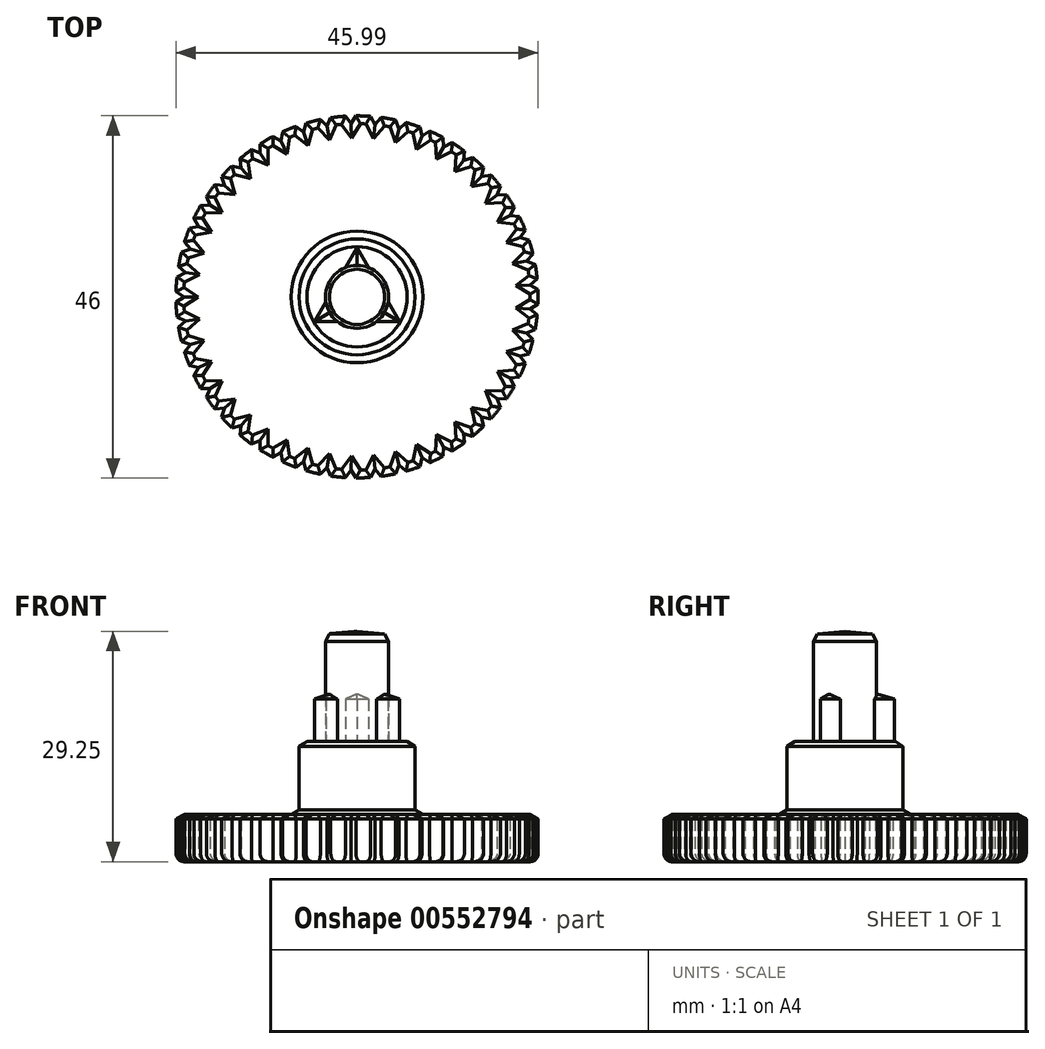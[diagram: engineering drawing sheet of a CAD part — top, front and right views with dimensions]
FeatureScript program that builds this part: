
annotation { "Feature Type Name" : "Feature", "Feature Type Description" : "" }
export const myFeature = defineFeature(function(context is Context, id is Id, definition is map)
    precondition{}
    {
        {
            var Q0;
            Q0=qCreatedBy(makeId("Front.planeOp"),FACE);
            var sketch = newSketch(context, id + "F0", { "sketchPlane" : qUnion([Q0])});
            skPoint(sketch, "E0.0", {"position": v(-5.65, 5.6) * mm});
            skLineSegment(sketch, "E1", {"start": v(-22, -9.25) * mm, "end": v(-22, -15.25) * mm});
            skLineSegment(sketch, "E2", {"start": v(-22, -15.25) * mm, "end": v(0, -15.25) * mm});
            skLineSegment(sketch, "E3", {"start": v(0, -15.25) * mm, "end": v(0, 14) * mm});
            skLineSegment(sketch, "E4", {"start": v(0, 14) * mm, "end": v(-4, 13.67) * mm});
            skLineSegment(sketch, "E5", {"start": v(-4, 13.67) * mm, "end": v(-4, 0) * mm});
            skLineSegment(sketch, "E6", {"start": v(-4, 0) * mm, "end": v(-7.37, 0) * mm});
            skLineSegment(sketch, "E7", {"start": v(-7.37, 0) * mm, "end": v(-7.37, -9.25) * mm});
            skLineSegment(sketch, "E8", {"start": v(-7.37, -9.25) * mm, "end": v(-22, -9.25) * mm});
            skSolve(sketch);
        }
        {
            var Q0;
            Q0=qSketchRegion(id+"F0",true);
            var Q1;
            Q1=sQuery(id+"F0.wireOp",EDGE,"E3");
            revolve(context, id + "F1", {"entities" : qUnion([Q0]), "axis" : qUnion([Q1]), "revolveType" : RevolveType.FULL});
        }
        {
            var Q0;
            Q0=makeQuery(id+"F1.opRevolve","SWEPT_FACE",FACE,{"disambiguationData":[OSD([sQuery(id+"F0.wireOp",EDGE,"E6")])]});
            var sketch = newSketch(context, id + "F2", { "sketchPlane" : qUnion([Q0])});
            skLineSegment(sketch, "E9", {"start": v(1.46, 3.72) * mm, "end": v(0, 6.25) * mm});
            skLineSegment(sketch, "E10", {"start": v(0, 6.25) * mm, "end": v(-1.46, 3.72) * mm});
            skLineSegment(sketch, "E11", {"start": v(-1.46, 3.72) * mm, "end": v(1.46, 3.72) * mm});
            skCircle(sketch, "E12", {"center": v(0, 0) * mm, "radius": 6.25 * mm, "construction": true});
            skCircle(sketch, "E13.0", {"center": v(0, 0) * mm, "radius": 4 * mm, "construction": true});
            skLineSegment(sketch, "E14.1.0", {"start": v(-5.41, -3.12) * mm, "end": v(-2.5, -3.12) * mm});
            skLineSegment(sketch, "E14.1.1", {"start": v(-3.95, -0.6) * mm, "end": v(-5.41, -3.12) * mm});
            skLineSegment(sketch, "E14.1.2", {"start": v(-2.5, -3.12) * mm, "end": v(-3.95, -0.6) * mm});
            skLineSegment(sketch, "E14.2.0", {"start": v(5.41, -3.12) * mm, "end": v(3.95, -0.6) * mm});
            skLineSegment(sketch, "E14.2.1", {"start": v(2.5, -3.12) * mm, "end": v(5.41, -3.12) * mm});
            skLineSegment(sketch, "E14.2.2", {"start": v(3.95, -0.6) * mm, "end": v(2.5, -3.12) * mm});
            skSolve(sketch);
        }
        {
            var Q0;
            Q0=qSketchRegion(id+"F2",true);
            extrude(context, id + "F3", {"entities" : qUnion([Q0]), "operationType" : NewBodyOperationType.ADD, "depth" : 6 * mm, "offsetDistance" : 25 * mm});
        }
        {
            var Q0;
            Q0=makeQuery(id+"F1.opRevolve","SWEPT_FACE",FACE,{"disambiguationData":[OSD([sQuery(id+"F0.wireOp",EDGE,"E2")])]});
            var sketch = newSketch(context, id + "F4", { "sketchPlane" : qUnion([Q0])});
            skCircle(sketch, "E15.0", {"center": v(0, 0) * mm, "radius": 22 * mm, "construction": true});
            skArc(sketch, "E16", {"start": v(-22.86, 2.54) * mm, "mid": v(-22.94, 1.6) * mm, "end": v(-23, 0.67) * mm});
            skLineSegment(sketch, "E17", {"start": v(-22.86, 2.54) * mm, "end": v(-21.79, 3.06) * mm});
            skLineSegment(sketch, "E18", {"start": v(-22, 0) * mm, "end": v(-21.79, 3.06) * mm});
            skLineSegment(sketch, "E19", {"start": v(-23, 0.67) * mm, "end": v(-22, 0) * mm});
            skLineSegment(sketch, "E20", {"start": v(-21.79, 3.06) * mm, "end": v(0, 0) * mm, "construction": true});
            skLineSegment(sketch, "E21", {"start": v(-22, 0) * mm, "end": v(0, 0) * mm, "construction": true});
            skLineSegment(sketch, "E22.1.0", {"start": v(-23, -0.67) * mm, "end": v(-22, 0) * mm});
            skArc(sketch, "E22.1.1", {"start": v(-23, -0.67) * mm, "mid": v(-22.94, -1.6) * mm, "end": v(-22.86, -2.54) * mm});
            skLineSegment(sketch, "E22.1.2", {"start": v(-22.86, -2.54) * mm, "end": v(-21.79, -3.06) * mm});
            skLineSegment(sketch, "E22.1.3", {"start": v(-21.79, -3.06) * mm, "end": v(-22, 0) * mm});
            skLineSegment(sketch, "E22.2.0", {"start": v(-22.67, -3.86) * mm, "end": v(-21.79, -3.06) * mm});
            skArc(sketch, "E22.2.1", {"start": v(-22.67, -3.86) * mm, "mid": v(-22.5, -4.78) * mm, "end": v(-22.28, -5.7) * mm});
            skLineSegment(sketch, "E22.2.2", {"start": v(-22.28, -5.7) * mm, "end": v(-21.15, -6.06) * mm});
            skLineSegment(sketch, "E22.2.3", {"start": v(-21.15, -6.06) * mm, "end": v(-21.79, -3.06) * mm});
            skLineSegment(sketch, "E22.3.0", {"start": v(-21.92, -6.98) * mm, "end": v(-21.15, -6.06) * mm});
            skArc(sketch, "E22.3.1", {"start": v(-21.92, -6.98) * mm, "mid": v(-21.61, -7.87) * mm, "end": v(-21.27, -8.74) * mm});
            skLineSegment(sketch, "E22.3.2", {"start": v(-21.27, -8.74) * mm, "end": v(-20.1, -8.95) * mm});
            skLineSegment(sketch, "E22.3.3", {"start": v(-20.1, -8.95) * mm, "end": v(-21.15, -6.06) * mm});
            skLineSegment(sketch, "E22.4.0", {"start": v(-20.73, -9.96) * mm, "end": v(-20.1, -8.95) * mm});
            skArc(sketch, "E22.4.1", {"start": v(-20.73, -9.96) * mm, "mid": v(-20.3, -10.8) * mm, "end": v(-19.85, -11.62) * mm});
            skLineSegment(sketch, "E22.4.2", {"start": v(-19.85, -11.62) * mm, "end": v(-18.66, -11.66) * mm});
            skLineSegment(sketch, "E22.4.3", {"start": v(-18.66, -11.66) * mm, "end": v(-20.1, -8.95) * mm});
            skLineSegment(sketch, "E22.5.0", {"start": v(-19.14, -12.75) * mm, "end": v(-18.66, -11.66) * mm});
            skArc(sketch, "E22.5.1", {"start": v(-19.14, -12.75) * mm, "mid": v(-18.6, -13.52) * mm, "end": v(-18.04, -14.27) * mm});
            skLineSegment(sketch, "E22.5.2", {"start": v(-18.04, -14.27) * mm, "end": v(-16.85, -14.14) * mm});
            skLineSegment(sketch, "E22.5.3", {"start": v(-16.85, -14.14) * mm, "end": v(-18.66, -11.66) * mm});
            skLineSegment(sketch, "E22.6.0", {"start": v(-17.18, -15.29) * mm, "end": v(-16.85, -14.14) * mm});
            skArc(sketch, "E22.6.1", {"start": v(-17.18, -15.29) * mm, "mid": v(-16.54, -15.98) * mm, "end": v(-15.88, -16.64) * mm});
            skLineSegment(sketch, "E22.6.2", {"start": v(-15.88, -16.64) * mm, "end": v(-14.72, -16.35) * mm});
            skLineSegment(sketch, "E22.6.3", {"start": v(-14.72, -16.35) * mm, "end": v(-16.85, -14.14) * mm});
            skLineSegment(sketch, "E22.7.0", {"start": v(-14.89, -17.53) * mm, "end": v(-14.72, -16.35) * mm});
            skArc(sketch, "E22.7.1", {"start": v(-14.89, -17.53) * mm, "mid": v(-14.16, -18.12) * mm, "end": v(-13.4, -18.69) * mm});
            skLineSegment(sketch, "E22.7.2", {"start": v(-13.4, -18.69) * mm, "end": v(-12.3, -18.24) * mm});
            skLineSegment(sketch, "E22.7.3", {"start": v(-12.3, -18.24) * mm, "end": v(-14.72, -16.35) * mm});
            skLineSegment(sketch, "E22.8.0", {"start": v(-12.3, -19.43) * mm, "end": v(-12.3, -18.24) * mm});
            skArc(sketch, "E22.8.1", {"start": v(-12.3, -19.43) * mm, "mid": v(-11.5, -19.92) * mm, "end": v(-10.68, -20.37) * mm});
            skLineSegment(sketch, "E22.8.2", {"start": v(-10.68, -20.37) * mm, "end": v(-9.64, -19.77) * mm});
            skLineSegment(sketch, "E22.8.3", {"start": v(-9.64, -19.77) * mm, "end": v(-12.3, -18.24) * mm});
            skLineSegment(sketch, "E22.9.0", {"start": v(-9.48, -20.96) * mm, "end": v(-9.64, -19.77) * mm});
            skArc(sketch, "E22.9.1", {"start": v(-9.48, -20.96) * mm, "mid": v(-8.62, -21.33) * mm, "end": v(-7.74, -21.66) * mm});
            skLineSegment(sketch, "E22.9.2", {"start": v(-7.74, -21.66) * mm, "end": v(-6.8, -20.92) * mm});
            skLineSegment(sketch, "E22.9.3", {"start": v(-6.8, -20.92) * mm, "end": v(-9.64, -19.77) * mm});
            skLineSegment(sketch, "E22.10.0", {"start": v(-6.47, -22.07) * mm, "end": v(-6.8, -20.92) * mm});
            skArc(sketch, "E22.10.1", {"start": v(-6.47, -22.07) * mm, "mid": v(-5.56, -22.32) * mm, "end": v(-4.65, -22.53) * mm});
            skLineSegment(sketch, "E22.10.2", {"start": v(-4.65, -22.53) * mm, "end": v(-3.82, -21.67) * mm});
            skLineSegment(sketch, "E22.10.3", {"start": v(-3.82, -21.67) * mm, "end": v(-6.8, -20.92) * mm});
            skLineSegment(sketch, "E22.11.0", {"start": v(-3.33, -22.76) * mm, "end": v(-3.82, -21.67) * mm});
            skArc(sketch, "E22.11.1", {"start": v(-3.33, -22.76) * mm, "mid": v(-2.4, -22.87) * mm, "end": v(-1.47, -22.95) * mm});
            skLineSegment(sketch, "E22.11.2", {"start": v(-1.47, -22.95) * mm, "end": v(-0.77, -21.99) * mm});
            skLineSegment(sketch, "E22.11.3", {"start": v(-0.77, -21.99) * mm, "end": v(-3.82, -21.67) * mm});
            skLineSegment(sketch, "E22.12.0", {"start": v(-0.13, -23) * mm, "end": v(-0.77, -21.99) * mm});
            skArc(sketch, "E22.12.1", {"start": v(-0.13, -23) * mm, "mid": v(0.8, -22.99) * mm, "end": v(1.74, -22.93) * mm});
            skLineSegment(sketch, "E22.12.2", {"start": v(1.74, -22.93) * mm, "end": v(2.3, -21.88) * mm});
            skLineSegment(sketch, "E22.12.3", {"start": v(2.3, -21.88) * mm, "end": v(-0.77, -21.99) * mm});
            skLineSegment(sketch, "E22.13.0", {"start": v(3.07, -22.8) * mm, "end": v(2.3, -21.88) * mm});
            skArc(sketch, "E22.13.1", {"start": v(3.07, -22.8) * mm, "mid": v(4, -22.65) * mm, "end": v(4.91, -22.47) * mm});
            skLineSegment(sketch, "E22.13.2", {"start": v(4.91, -22.47) * mm, "end": v(5.32, -21.35) * mm});
            skLineSegment(sketch, "E22.13.3", {"start": v(5.32, -21.35) * mm, "end": v(2.3, -21.88) * mm});
            skLineSegment(sketch, "E22.14.0", {"start": v(6.2, -22.15) * mm, "end": v(5.32, -21.35) * mm});
            skArc(sketch, "E22.14.1", {"start": v(6.2, -22.15) * mm, "mid": v(7.1, -21.87) * mm, "end": v(8, -21.57) * mm});
            skLineSegment(sketch, "E22.14.2", {"start": v(8, -21.57) * mm, "end": v(8.24, -20.4) * mm});
            skLineSegment(sketch, "E22.14.3", {"start": v(8.24, -20.4) * mm, "end": v(5.32, -21.35) * mm});
            skLineSegment(sketch, "E22.15.0", {"start": v(9.23, -21.07) * mm, "end": v(8.24, -20.4) * mm});
            skArc(sketch, "E22.15.1", {"start": v(9.23, -21.07) * mm, "mid": v(10.08, -20.67) * mm, "end": v(10.92, -20.24) * mm});
            skLineSegment(sketch, "E22.15.2", {"start": v(10.92, -20.24) * mm, "end": v(11, -19.05) * mm});
            skLineSegment(sketch, "E22.15.3", {"start": v(11, -19.05) * mm, "end": v(8.24, -20.4) * mm});
            skLineSegment(sketch, "E22.16.0", {"start": v(12.07, -19.58) * mm, "end": v(11, -19.05) * mm});
            skArc(sketch, "E22.16.1", {"start": v(12.07, -19.58) * mm, "mid": v(12.86, -19.07) * mm, "end": v(13.63, -18.53) * mm});
            skLineSegment(sketch, "E22.16.2", {"start": v(13.63, -18.53) * mm, "end": v(13.54, -17.34) * mm});
            skLineSegment(sketch, "E22.16.3", {"start": v(13.54, -17.34) * mm, "end": v(11, -19.05) * mm});
            skLineSegment(sketch, "E22.17.0", {"start": v(14.68, -17.7) * mm, "end": v(13.54, -17.34) * mm});
            skArc(sketch, "E22.17.1", {"start": v(14.68, -17.7) * mm, "mid": v(15.4, -17.1) * mm, "end": v(16.07, -16.45) * mm});
            skLineSegment(sketch, "E22.17.2", {"start": v(16.07, -16.45) * mm, "end": v(15.83, -15.28) * mm});
            skLineSegment(sketch, "E22.17.3", {"start": v(15.83, -15.28) * mm, "end": v(13.54, -17.34) * mm});
            skLineSegment(sketch, "E22.18.0", {"start": v(17, -15.49) * mm, "end": v(15.83, -15.28) * mm});
            skArc(sketch, "E22.18.1", {"start": v(17, -15.49) * mm, "mid": v(17.62, -14.78) * mm, "end": v(18.2, -14.05) * mm});
            skLineSegment(sketch, "E22.18.2", {"start": v(18.2, -14.05) * mm, "end": v(17.8, -12.93) * mm});
            skLineSegment(sketch, "E22.18.3", {"start": v(17.8, -12.93) * mm, "end": v(15.83, -15.28) * mm});
            skLineSegment(sketch, "E22.19.0", {"start": v(19, -12.97) * mm, "end": v(17.8, -12.93) * mm});
            skArc(sketch, "E22.19.1", {"start": v(19, -12.97) * mm, "mid": v(19.5, -12.19) * mm, "end": v(19.99, -11.38) * mm});
            skLineSegment(sketch, "E22.19.2", {"start": v(19.99, -11.38) * mm, "end": v(19.42, -10.33) * mm});
            skLineSegment(sketch, "E22.19.3", {"start": v(19.42, -10.33) * mm, "end": v(17.8, -12.93) * mm});
            skLineSegment(sketch, "E22.20.0", {"start": v(20.61, -10.2) * mm, "end": v(19.42, -10.33) * mm});
            skArc(sketch, "E22.20.1", {"start": v(20.61, -10.2) * mm, "mid": v(21.01, -9.35) * mm, "end": v(21.38, -8.5) * mm});
            skLineSegment(sketch, "E22.20.2", {"start": v(21.38, -8.5) * mm, "end": v(20.67, -7.52) * mm});
            skLineSegment(sketch, "E22.20.3", {"start": v(20.67, -7.52) * mm, "end": v(19.42, -10.33) * mm});
            skLineSegment(sketch, "E22.21.0", {"start": v(21.83, -7.24) * mm, "end": v(20.67, -7.52) * mm});
            skArc(sketch, "E22.21.1", {"start": v(21.83, -7.24) * mm, "mid": v(22.1, -6.34) * mm, "end": v(22.35, -5.43) * mm});
            skLineSegment(sketch, "E22.21.2", {"start": v(22.35, -5.43) * mm, "end": v(21.52, -4.57) * mm});
            skLineSegment(sketch, "E22.21.3", {"start": v(21.52, -4.57) * mm, "end": v(20.67, -7.52) * mm});
            skLineSegment(sketch, "E22.22.0", {"start": v(22.63, -4.13) * mm, "end": v(21.52, -4.57) * mm});
            skArc(sketch, "E22.22.1", {"start": v(22.63, -4.13) * mm, "mid": v(22.78, -3.2) * mm, "end": v(22.89, -2.27) * mm});
            skLineSegment(sketch, "E22.22.2", {"start": v(22.89, -2.27) * mm, "end": v(21.95, -1.53) * mm});
            skLineSegment(sketch, "E22.22.3", {"start": v(21.95, -1.53) * mm, "end": v(21.52, -4.57) * mm});
            skLineSegment(sketch, "E22.23.0", {"start": v(22.98, -0.94) * mm, "end": v(21.95, -1.53) * mm});
            skArc(sketch, "E22.23.1", {"start": v(22.98, -0.94) * mm, "mid": v(23, 0) * mm, "end": v(22.98, 0.94) * mm});
            skLineSegment(sketch, "E22.23.2", {"start": v(22.98, 0.94) * mm, "end": v(21.95, 1.53) * mm});
            skLineSegment(sketch, "E22.23.3", {"start": v(21.95, 1.53) * mm, "end": v(21.95, -1.53) * mm});
            skLineSegment(sketch, "E22.24.0", {"start": v(22.89, 2.27) * mm, "end": v(21.95, 1.53) * mm});
            skArc(sketch, "E22.24.1", {"start": v(22.89, 2.27) * mm, "mid": v(22.78, 3.2) * mm, "end": v(22.63, 4.13) * mm});
            skLineSegment(sketch, "E22.24.2", {"start": v(22.63, 4.13) * mm, "end": v(21.52, 4.57) * mm});
            skLineSegment(sketch, "E22.24.3", {"start": v(21.52, 4.57) * mm, "end": v(21.95, 1.53) * mm});
            skLineSegment(sketch, "E22.25.0", {"start": v(22.35, 5.43) * mm, "end": v(21.52, 4.57) * mm});
            skArc(sketch, "E22.25.1", {"start": v(22.35, 5.43) * mm, "mid": v(22.1, 6.34) * mm, "end": v(21.83, 7.24) * mm});
            skLineSegment(sketch, "E22.25.2", {"start": v(21.83, 7.24) * mm, "end": v(20.67, 7.52) * mm});
            skLineSegment(sketch, "E22.25.3", {"start": v(20.67, 7.52) * mm, "end": v(21.52, 4.57) * mm});
            skLineSegment(sketch, "E22.26.0", {"start": v(21.38, 8.5) * mm, "end": v(20.67, 7.52) * mm});
            skArc(sketch, "E22.26.1", {"start": v(21.38, 8.5) * mm, "mid": v(21.01, 9.35) * mm, "end": v(20.61, 10.2) * mm});
            skLineSegment(sketch, "E22.26.2", {"start": v(20.61, 10.2) * mm, "end": v(19.42, 10.33) * mm});
            skLineSegment(sketch, "E22.26.3", {"start": v(19.42, 10.33) * mm, "end": v(20.67, 7.52) * mm});
            skLineSegment(sketch, "E22.27.0", {"start": v(19.99, 11.38) * mm, "end": v(19.42, 10.33) * mm});
            skArc(sketch, "E22.27.1", {"start": v(19.99, 11.38) * mm, "mid": v(19.5, 12.19) * mm, "end": v(19, 12.97) * mm});
            skLineSegment(sketch, "E22.27.2", {"start": v(19, 12.97) * mm, "end": v(17.8, 12.93) * mm});
            skLineSegment(sketch, "E22.27.3", {"start": v(17.8, 12.93) * mm, "end": v(19.42, 10.33) * mm});
            skLineSegment(sketch, "E22.28.0", {"start": v(18.2, 14.05) * mm, "end": v(17.8, 12.93) * mm});
            skArc(sketch, "E22.28.1", {"start": v(18.2, 14.05) * mm, "mid": v(17.62, 14.78) * mm, "end": v(17, 15.49) * mm});
            skLineSegment(sketch, "E22.28.2", {"start": v(17, 15.49) * mm, "end": v(15.83, 15.28) * mm});
            skLineSegment(sketch, "E22.28.3", {"start": v(15.83, 15.28) * mm, "end": v(17.8, 12.93) * mm});
            skLineSegment(sketch, "E22.29.0", {"start": v(16.07, 16.45) * mm, "end": v(15.83, 15.28) * mm});
            skArc(sketch, "E22.29.1", {"start": v(16.07, 16.45) * mm, "mid": v(15.4, 17.1) * mm, "end": v(14.68, 17.7) * mm});
            skLineSegment(sketch, "E22.29.2", {"start": v(14.68, 17.7) * mm, "end": v(13.54, 17.34) * mm});
            skLineSegment(sketch, "E22.29.3", {"start": v(13.54, 17.34) * mm, "end": v(15.83, 15.28) * mm});
            skLineSegment(sketch, "E22.30.0", {"start": v(13.63, 18.53) * mm, "end": v(13.54, 17.34) * mm});
            skArc(sketch, "E22.30.1", {"start": v(13.63, 18.53) * mm, "mid": v(12.86, 19.07) * mm, "end": v(12.07, 19.58) * mm});
            skLineSegment(sketch, "E22.30.2", {"start": v(12.07, 19.58) * mm, "end": v(11, 19.05) * mm});
            skLineSegment(sketch, "E22.30.3", {"start": v(11, 19.05) * mm, "end": v(13.54, 17.34) * mm});
            skLineSegment(sketch, "E22.31.0", {"start": v(10.92, 20.24) * mm, "end": v(11, 19.05) * mm});
            skArc(sketch, "E22.31.1", {"start": v(10.92, 20.24) * mm, "mid": v(10.08, 20.67) * mm, "end": v(9.23, 21.07) * mm});
            skLineSegment(sketch, "E22.31.2", {"start": v(9.23, 21.07) * mm, "end": v(8.24, 20.4) * mm});
            skLineSegment(sketch, "E22.31.3", {"start": v(8.24, 20.4) * mm, "end": v(11, 19.05) * mm});
            skLineSegment(sketch, "E22.32.0", {"start": v(8, 21.57) * mm, "end": v(8.24, 20.4) * mm});
            skArc(sketch, "E22.32.1", {"start": v(8, 21.57) * mm, "mid": v(7.1, 21.87) * mm, "end": v(6.2, 22.15) * mm});
            skLineSegment(sketch, "E22.32.2", {"start": v(6.2, 22.15) * mm, "end": v(5.32, 21.35) * mm});
            skLineSegment(sketch, "E22.32.3", {"start": v(5.32, 21.35) * mm, "end": v(8.24, 20.4) * mm});
            skLineSegment(sketch, "E22.33.0", {"start": v(4.91, 22.47) * mm, "end": v(5.32, 21.35) * mm});
            skArc(sketch, "E22.33.1", {"start": v(4.91, 22.47) * mm, "mid": v(4, 22.65) * mm, "end": v(3.07, 22.8) * mm});
            skLineSegment(sketch, "E22.33.2", {"start": v(3.07, 22.8) * mm, "end": v(2.3, 21.88) * mm});
            skLineSegment(sketch, "E22.33.3", {"start": v(2.3, 21.88) * mm, "end": v(5.32, 21.35) * mm});
            skLineSegment(sketch, "E22.34.0", {"start": v(1.74, 22.93) * mm, "end": v(2.3, 21.88) * mm});
            skArc(sketch, "E22.34.1", {"start": v(1.74, 22.93) * mm, "mid": v(0.8, 22.99) * mm, "end": v(-0.13, 23) * mm});
            skLineSegment(sketch, "E22.34.2", {"start": v(-0.13, 23) * mm, "end": v(-0.77, 21.99) * mm});
            skLineSegment(sketch, "E22.34.3", {"start": v(-0.77, 21.99) * mm, "end": v(2.3, 21.88) * mm});
            skLineSegment(sketch, "E22.35.0", {"start": v(-1.47, 22.95) * mm, "end": v(-0.77, 21.99) * mm});
            skArc(sketch, "E22.35.1", {"start": v(-1.47, 22.95) * mm, "mid": v(-2.4, 22.87) * mm, "end": v(-3.33, 22.76) * mm});
            skLineSegment(sketch, "E22.35.2", {"start": v(-3.33, 22.76) * mm, "end": v(-3.82, 21.67) * mm});
            skLineSegment(sketch, "E22.35.3", {"start": v(-3.82, 21.67) * mm, "end": v(-0.77, 21.99) * mm});
            skLineSegment(sketch, "E22.36.0", {"start": v(-4.65, 22.53) * mm, "end": v(-3.82, 21.67) * mm});
            skArc(sketch, "E22.36.1", {"start": v(-4.65, 22.53) * mm, "mid": v(-5.56, 22.32) * mm, "end": v(-6.47, 22.07) * mm});
            skLineSegment(sketch, "E22.36.2", {"start": v(-6.47, 22.07) * mm, "end": v(-6.8, 20.92) * mm});
            skLineSegment(sketch, "E22.36.3", {"start": v(-6.8, 20.92) * mm, "end": v(-3.82, 21.67) * mm});
            skLineSegment(sketch, "E22.37.0", {"start": v(-7.74, 21.66) * mm, "end": v(-6.8, 20.92) * mm});
            skArc(sketch, "E22.37.1", {"start": v(-7.74, 21.66) * mm, "mid": v(-8.62, 21.33) * mm, "end": v(-9.48, 20.96) * mm});
            skLineSegment(sketch, "E22.37.2", {"start": v(-9.48, 20.96) * mm, "end": v(-9.64, 19.77) * mm});
            skLineSegment(sketch, "E22.37.3", {"start": v(-9.64, 19.77) * mm, "end": v(-6.8, 20.92) * mm});
            skLineSegment(sketch, "E22.38.0", {"start": v(-10.68, 20.37) * mm, "end": v(-9.64, 19.77) * mm});
            skArc(sketch, "E22.38.1", {"start": v(-10.68, 20.37) * mm, "mid": v(-11.5, 19.92) * mm, "end": v(-12.3, 19.43) * mm});
            skLineSegment(sketch, "E22.38.2", {"start": v(-12.3, 19.43) * mm, "end": v(-12.3, 18.24) * mm});
            skLineSegment(sketch, "E22.38.3", {"start": v(-12.3, 18.24) * mm, "end": v(-9.64, 19.77) * mm});
            skLineSegment(sketch, "E22.39.0", {"start": v(-13.4, 18.69) * mm, "end": v(-12.3, 18.24) * mm});
            skArc(sketch, "E22.39.1", {"start": v(-13.4, 18.69) * mm, "mid": v(-14.16, 18.12) * mm, "end": v(-14.89, 17.53) * mm});
            skLineSegment(sketch, "E22.39.2", {"start": v(-14.89, 17.53) * mm, "end": v(-14.72, 16.35) * mm});
            skLineSegment(sketch, "E22.39.3", {"start": v(-14.72, 16.35) * mm, "end": v(-12.3, 18.24) * mm});
            skLineSegment(sketch, "E22.40.0", {"start": v(-15.88, 16.64) * mm, "end": v(-14.72, 16.35) * mm});
            skArc(sketch, "E22.40.1", {"start": v(-15.88, 16.64) * mm, "mid": v(-16.54, 15.98) * mm, "end": v(-17.18, 15.29) * mm});
            skLineSegment(sketch, "E22.40.2", {"start": v(-17.18, 15.29) * mm, "end": v(-16.85, 14.14) * mm});
            skLineSegment(sketch, "E22.40.3", {"start": v(-16.85, 14.14) * mm, "end": v(-14.72, 16.35) * mm});
            skLineSegment(sketch, "E22.41.0", {"start": v(-18.04, 14.27) * mm, "end": v(-16.85, 14.14) * mm});
            skArc(sketch, "E22.41.1", {"start": v(-18.04, 14.27) * mm, "mid": v(-18.6, 13.52) * mm, "end": v(-19.14, 12.75) * mm});
            skLineSegment(sketch, "E22.41.2", {"start": v(-19.14, 12.75) * mm, "end": v(-18.66, 11.66) * mm});
            skLineSegment(sketch, "E22.41.3", {"start": v(-18.66, 11.66) * mm, "end": v(-16.85, 14.14) * mm});
            skLineSegment(sketch, "E22.42.0", {"start": v(-19.85, 11.62) * mm, "end": v(-18.66, 11.66) * mm});
            skArc(sketch, "E22.42.1", {"start": v(-19.85, 11.62) * mm, "mid": v(-20.3, 10.8) * mm, "end": v(-20.73, 9.96) * mm});
            skLineSegment(sketch, "E22.42.2", {"start": v(-20.73, 9.96) * mm, "end": v(-20.1, 8.95) * mm});
            skLineSegment(sketch, "E22.42.3", {"start": v(-20.1, 8.95) * mm, "end": v(-18.66, 11.66) * mm});
            skLineSegment(sketch, "E22.43.0", {"start": v(-21.27, 8.74) * mm, "end": v(-20.1, 8.95) * mm});
            skArc(sketch, "E22.43.1", {"start": v(-21.27, 8.74) * mm, "mid": v(-21.61, 7.87) * mm, "end": v(-21.92, 6.98) * mm});
            skLineSegment(sketch, "E22.43.2", {"start": v(-21.92, 6.98) * mm, "end": v(-21.15, 6.06) * mm});
            skLineSegment(sketch, "E22.43.3", {"start": v(-21.15, 6.06) * mm, "end": v(-20.1, 8.95) * mm});
            skLineSegment(sketch, "E22.44.0", {"start": v(-22.28, 5.7) * mm, "end": v(-21.15, 6.06) * mm});
            skArc(sketch, "E22.44.1", {"start": v(-22.28, 5.7) * mm, "mid": v(-22.5, 4.78) * mm, "end": v(-22.67, 3.86) * mm});
            skLineSegment(sketch, "E22.44.2", {"start": v(-22.67, 3.86) * mm, "end": v(-21.79, 3.06) * mm});
            skLineSegment(sketch, "E22.44.3", {"start": v(-21.79, 3.06) * mm, "end": v(-21.15, 6.06) * mm});
            skSolve(sketch);
        }
        {
            var Q0;
            Q0=qSketchRegion(id+"F4",true);
            var Q1;
            Q1=makeQuery(id+"F1.opRevolve","SWEPT_FACE",FACE,{"disambiguationData":[OSD([sQuery(id+"F0.wireOp",EDGE,"E8")])]});
            extrude(context, id + "F5", {"entities" : qUnion([Q0]), "operationType" : NewBodyOperationType.ADD, "endBound" : BoundingType.UP_TO_SURFACE, "oppositeDirection" : true, "depth" : 25 * mm, "endBoundEntityFace" : qUnion([Q1]), "offsetDistance" : 25 * mm});
        }
        {
            var Q0;
            {var subQ0=sQuery(id+"F0.wireOp",EDGE,"E8");Q0=makeQuery(id+"F5.boolean.opBoolean","MERGE",FACE,{"derivedFrom":[makeQuery(id+"F1.opRevolve","SWEPT_FACE",FACE,{"disambiguationData":[OSD([subQ0])]}),makeQuery(id+"F5.opExtrude","CAP_FACE",FACE,{"disambiguationData":[OSD([subQ0])],"isStart":false})]});}
            var Q1;
            Q1=makeQuery(id+"F1.opRevolve","SWEPT_EDGE",EDGE,{"disambiguationData":[OSD([sQuery(id+"F0.wireOp",EDGE,"E6"),sQuery(id+"F0.wireOp",EDGE,"E7")])]});
            var Q2;
            Q2=makeQuery(id+"F1.opRevolve","SWEPT_EDGE",EDGE,{"disambiguationData":[OSD([sQuery(id+"F0.wireOp",EDGE,"E4"),sQuery(id+"F0.wireOp",EDGE,"E5")])]});
            var Q3;
            Q3=makeQuery(id+"F3.opExtrude","CAP_EDGE",EDGE,{"disambiguationData":[OSD([sQuery(id+"F2.wireOp",EDGE,"E14.2.0")])],"isStart":false});
            var Q4;
            Q4=makeQuery(id+"F3.opExtrude","CAP_EDGE",EDGE,{"disambiguationData":[OSD([sQuery(id+"F2.wireOp",EDGE,"E14.2.1")])],"isStart":false});
            var Q5;
            Q5=makeQuery(id+"F3.opExtrude","CAP_EDGE",EDGE,{"disambiguationData":[OSD([sQuery(id+"F2.wireOp",EDGE,"E9")])],"isStart":false});
            var Q6;
            Q6=makeQuery(id+"F3.opExtrude","CAP_EDGE",EDGE,{"disambiguationData":[OSD([sQuery(id+"F2.wireOp",EDGE,"E10")])],"isStart":false});
            var Q7;
            Q7=makeQuery(id+"F3.opExtrude","CAP_EDGE",EDGE,{"disambiguationData":[OSD([sQuery(id+"F2.wireOp",EDGE,"E14.1.0")])],"isStart":false});
            var Q8;
            Q8=makeQuery(id+"F3.opExtrude","CAP_EDGE",EDGE,{"disambiguationData":[OSD([sQuery(id+"F2.wireOp",EDGE,"E14.1.1")])],"isStart":false});
            chamfer(context, id + "F6", {"entities" : qUnion([Q0, Q1, Q2, Q3, Q4, Q5, Q6, Q7, Q8]), "chamferType" : ChamferType.OFFSET_ANGLE, "width" : 1 * mm, "oppositeDirection" : false, "angle" : 30 * degree, "tangentPropagation" : true});
        }
        {
            var Q0;
            Q0=makeQuery(id+"F5.boolean.opBoolean","MERGE",FACE,{"derivedFrom":[makeQuery(id+"F1.opRevolve","SWEPT_FACE",FACE,{"disambiguationData":[OSD([sQuery(id+"F0.wireOp",EDGE,"E2")])]}),makeQuery(id+"F5.opExtrude","CAP_FACE",FACE,{"disambiguationData":[OSD([sQuery(id+"F4.wireOp",EDGE,"E16"),sQuery(id+"F4.wireOp",EDGE,"E17"),sQuery(id+"F4.wireOp",EDGE,"E19"),sQuery(id+"F4.wireOp",EDGE,"E22.1.0"),sQuery(id+"F4.wireOp",EDGE,"E22.1.1"),sQuery(id+"F4.wireOp",EDGE,"E22.1.2"),sQuery(id+"F4.wireOp",EDGE,"E22.2.0"),sQuery(id+"F4.wireOp",EDGE,"E22.2.1"),sQuery(id+"F4.wireOp",EDGE,"E22.2.2"),sQuery(id+"F4.wireOp",EDGE,"E22.3.0"),sQuery(id+"F4.wireOp",EDGE,"E22.3.1"),sQuery(id+"F4.wireOp",EDGE,"E22.3.2"),sQuery(id+"F4.wireOp",EDGE,"E22.4.0"),sQuery(id+"F4.wireOp",EDGE,"E22.4.1"),sQuery(id+"F4.wireOp",EDGE,"E22.4.2"),sQuery(id+"F4.wireOp",EDGE,"E22.5.0"),sQuery(id+"F4.wireOp",EDGE,"E22.5.1"),sQuery(id+"F4.wireOp",EDGE,"E22.5.2"),sQuery(id+"F4.wireOp",EDGE,"E22.6.0"),sQuery(id+"F4.wireOp",EDGE,"E22.6.1"),sQuery(id+"F4.wireOp",EDGE,"E22.6.2"),sQuery(id+"F4.wireOp",EDGE,"E22.7.0"),sQuery(id+"F4.wireOp",EDGE,"E22.7.1"),sQuery(id+"F4.wireOp",EDGE,"E22.7.2"),sQuery(id+"F4.wireOp",EDGE,"E22.8.0"),sQuery(id+"F4.wireOp",EDGE,"E22.8.1"),sQuery(id+"F4.wireOp",EDGE,"E22.8.2"),sQuery(id+"F4.wireOp",EDGE,"E22.9.0"),sQuery(id+"F4.wireOp",EDGE,"E22.9.1"),sQuery(id+"F4.wireOp",EDGE,"E22.9.2"),sQuery(id+"F4.wireOp",EDGE,"E22.10.0"),sQuery(id+"F4.wireOp",EDGE,"E22.10.1"),sQuery(id+"F4.wireOp",EDGE,"E22.10.2"),sQuery(id+"F4.wireOp",EDGE,"E22.11.0"),sQuery(id+"F4.wireOp",EDGE,"E22.11.1"),sQuery(id+"F4.wireOp",EDGE,"E22.11.2"),sQuery(id+"F4.wireOp",EDGE,"E22.12.0"),sQuery(id+"F4.wireOp",EDGE,"E22.12.1"),sQuery(id+"F4.wireOp",EDGE,"E22.12.2"),sQuery(id+"F4.wireOp",EDGE,"E22.13.0"),sQuery(id+"F4.wireOp",EDGE,"E22.13.1"),sQuery(id+"F4.wireOp",EDGE,"E22.13.2"),sQuery(id+"F4.wireOp",EDGE,"E22.14.0"),sQuery(id+"F4.wireOp",EDGE,"E22.14.1"),sQuery(id+"F4.wireOp",EDGE,"E22.14.2"),sQuery(id+"F4.wireOp",EDGE,"E22.15.0"),sQuery(id+"F4.wireOp",EDGE,"E22.15.1"),sQuery(id+"F4.wireOp",EDGE,"E22.15.2"),sQuery(id+"F4.wireOp",EDGE,"E22.16.0"),sQuery(id+"F4.wireOp",EDGE,"E22.16.1"),sQuery(id+"F4.wireOp",EDGE,"E22.16.2"),sQuery(id+"F4.wireOp",EDGE,"E22.17.0"),sQuery(id+"F4.wireOp",EDGE,"E22.17.1"),sQuery(id+"F4.wireOp",EDGE,"E22.17.2"),sQuery(id+"F4.wireOp",EDGE,"E22.18.0"),sQuery(id+"F4.wireOp",EDGE,"E22.18.1"),sQuery(id+"F4.wireOp",EDGE,"E22.18.2"),sQuery(id+"F4.wireOp",EDGE,"E22.19.0"),sQuery(id+"F4.wireOp",EDGE,"E22.19.1"),sQuery(id+"F4.wireOp",EDGE,"E22.19.2"),sQuery(id+"F4.wireOp",EDGE,"E22.20.0"),sQuery(id+"F4.wireOp",EDGE,"E22.20.1"),sQuery(id+"F4.wireOp",EDGE,"E22.20.2"),sQuery(id+"F4.wireOp",EDGE,"E22.21.0"),sQuery(id+"F4.wireOp",EDGE,"E22.21.1"),sQuery(id+"F4.wireOp",EDGE,"E22.21.2"),sQuery(id+"F4.wireOp",EDGE,"E22.22.0"),sQuery(id+"F4.wireOp",EDGE,"E22.22.1"),sQuery(id+"F4.wireOp",EDGE,"E22.22.2"),sQuery(id+"F4.wireOp",EDGE,"E22.23.0"),sQuery(id+"F4.wireOp",EDGE,"E22.23.1"),sQuery(id+"F4.wireOp",EDGE,"E22.23.2"),sQuery(id+"F4.wireOp",EDGE,"E22.24.0"),sQuery(id+"F4.wireOp",EDGE,"E22.24.1"),sQuery(id+"F4.wireOp",EDGE,"E22.24.2"),sQuery(id+"F4.wireOp",EDGE,"E22.25.0"),sQuery(id+"F4.wireOp",EDGE,"E22.25.1"),sQuery(id+"F4.wireOp",EDGE,"E22.25.2"),sQuery(id+"F4.wireOp",EDGE,"E22.26.0"),sQuery(id+"F4.wireOp",EDGE,"E22.26.1"),sQuery(id+"F4.wireOp",EDGE,"E22.26.2"),sQuery(id+"F4.wireOp",EDGE,"E22.27.0"),sQuery(id+"F4.wireOp",EDGE,"E22.27.1"),sQuery(id+"F4.wireOp",EDGE,"E22.27.2"),sQuery(id+"F4.wireOp",EDGE,"E22.28.0"),sQuery(id+"F4.wireOp",EDGE,"E22.28.1"),sQuery(id+"F4.wireOp",EDGE,"E22.28.2"),sQuery(id+"F4.wireOp",EDGE,"E22.29.0"),sQuery(id+"F4.wireOp",EDGE,"E22.29.1"),sQuery(id+"F4.wireOp",EDGE,"E22.29.2"),sQuery(id+"F4.wireOp",EDGE,"E22.30.0"),sQuery(id+"F4.wireOp",EDGE,"E22.30.1"),sQuery(id+"F4.wireOp",EDGE,"E22.30.2"),sQuery(id+"F4.wireOp",EDGE,"E22.31.0"),sQuery(id+"F4.wireOp",EDGE,"E22.31.1"),sQuery(id+"F4.wireOp",EDGE,"E22.31.2"),sQuery(id+"F4.wireOp",EDGE,"E22.32.0"),sQuery(id+"F4.wireOp",EDGE,"E22.32.1"),sQuery(id+"F4.wireOp",EDGE,"E22.32.2"),sQuery(id+"F4.wireOp",EDGE,"E22.33.0"),sQuery(id+"F4.wireOp",EDGE,"E22.33.1"),sQuery(id+"F4.wireOp",EDGE,"E22.33.2"),sQuery(id+"F4.wireOp",EDGE,"E22.34.0"),sQuery(id+"F4.wireOp",EDGE,"E22.34.1"),sQuery(id+"F4.wireOp",EDGE,"E22.34.2"),sQuery(id+"F4.wireOp",EDGE,"E22.35.0"),sQuery(id+"F4.wireOp",EDGE,"E22.35.1"),sQuery(id+"F4.wireOp",EDGE,"E22.35.2"),sQuery(id+"F4.wireOp",EDGE,"E22.36.0"),sQuery(id+"F4.wireOp",EDGE,"E22.36.1"),sQuery(id+"F4.wireOp",EDGE,"E22.36.2"),sQuery(id+"F4.wireOp",EDGE,"E22.37.0"),sQuery(id+"F4.wireOp",EDGE,"E22.37.1"),sQuery(id+"F4.wireOp",EDGE,"E22.37.2"),sQuery(id+"F4.wireOp",EDGE,"E22.38.0"),sQuery(id+"F4.wireOp",EDGE,"E22.38.1"),sQuery(id+"F4.wireOp",EDGE,"E22.38.2"),sQuery(id+"F4.wireOp",EDGE,"E22.39.0"),sQuery(id+"F4.wireOp",EDGE,"E22.39.1"),sQuery(id+"F4.wireOp",EDGE,"E22.39.2"),sQuery(id+"F4.wireOp",EDGE,"E22.40.0"),sQuery(id+"F4.wireOp",EDGE,"E22.40.1"),sQuery(id+"F4.wireOp",EDGE,"E22.40.2"),sQuery(id+"F4.wireOp",EDGE,"E22.41.0"),sQuery(id+"F4.wireOp",EDGE,"E22.41.1"),sQuery(id+"F4.wireOp",EDGE,"E22.41.2"),sQuery(id+"F4.wireOp",EDGE,"E22.42.0"),sQuery(id+"F4.wireOp",EDGE,"E22.42.1"),sQuery(id+"F4.wireOp",EDGE,"E22.42.2"),sQuery(id+"F4.wireOp",EDGE,"E22.43.0"),sQuery(id+"F4.wireOp",EDGE,"E22.43.1"),sQuery(id+"F4.wireOp",EDGE,"E22.43.2"),sQuery(id+"F4.wireOp",EDGE,"E22.44.0"),sQuery(id+"F4.wireOp",EDGE,"E22.44.1"),sQuery(id+"F4.wireOp",EDGE,"E22.44.2")])],"isStart":true})]});
            fillet(context, id + "F7", {"entities" : qUnion([Q0]), "radius" : 1 * mm, "tangentPropagation" : true, "allowEdgeOverflow" : false});
        }
    });
